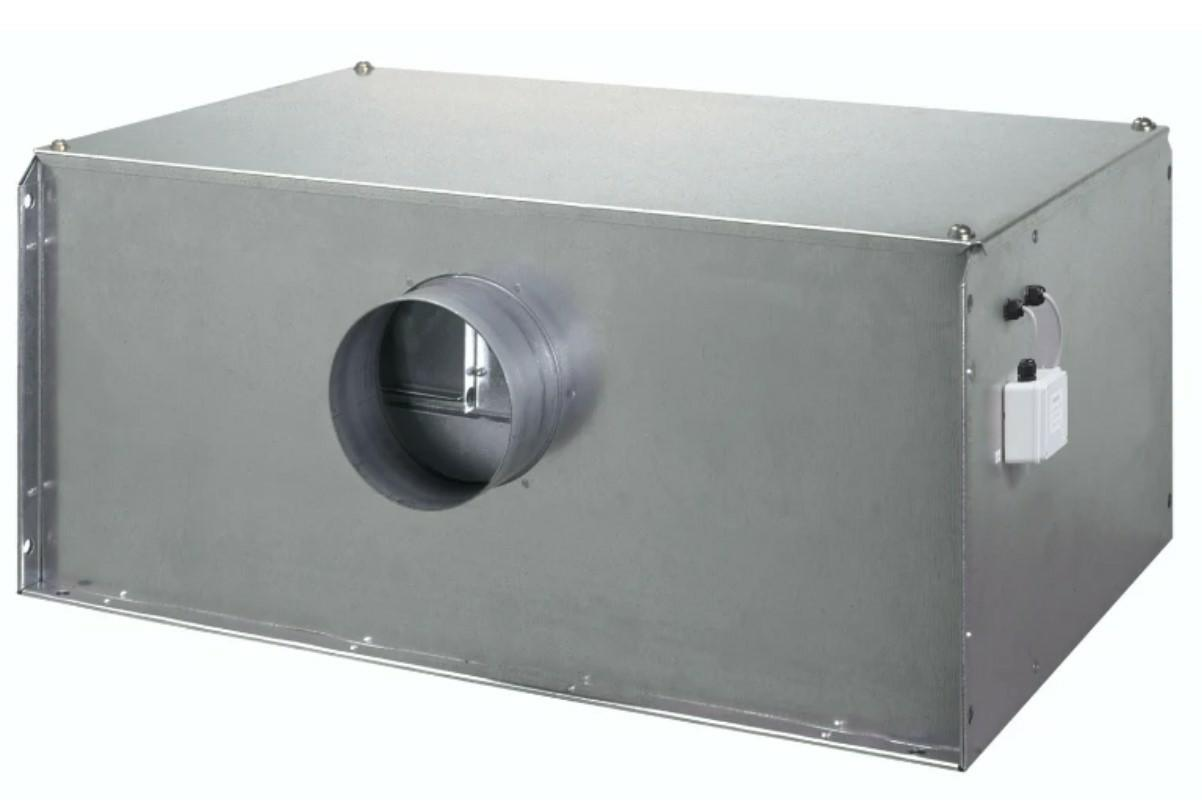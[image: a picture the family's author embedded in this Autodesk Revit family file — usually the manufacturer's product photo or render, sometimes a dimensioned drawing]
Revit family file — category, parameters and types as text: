
# Revit family: CADS_Vent-Axia_MechEquip_Fan_ATQ - EXTRACT
name_source: partatom
category: Mechanical Equipment
units: mm (PartAtom-declared; Revit-internal decimal feet)

## family parameters
Classification = None
Cut with Voids When Loaded = No
Host = Face
OmniClass Number = 23.75.35.17.11
OmniClass Title = Fans for Air Ductwork
Part Type = Normal
Room Calculation Point = No
Round Connector Dimension = Use Diameter
Shared = No

## types (9) — shared parameters
AirflowRateRange = 0.0 L/s
AssemblyPlace = UNKNOWN
AssetType = FIXED
Default Elevation = 1219 mm
DurationUnit = Year
ExteriorInsulation = No
Fitting Type = Ignore
GrossWeight = 0.00 kg
HasProtectiveEarth = No
IsExtendedWarranty = No
ManufacturerAddress = Fleming Way
Crawley 
RH10 9YX
Quantity = 1
RatedCurrent = 0 A
RatedVoltage = 0 V
Status = New
WorkingPressure = 0.0 Pa
zero-valued in all types: CADS_Index, CADS_Usage, ExpectedServiceLife, H, NumberOfPoles, OutOffset, W

## per-type parameters (varying)
| type | EBHoffset | EBVoffset | L | ModelNumber | ModelReference | NominalDiameter | NominalHeight | NominalLength | NominalWidth | Size | SpigotCLHeight | Type Image |
| ATQ10012D | 206 mm | 80 mm | 590 mm  [stored 1.9357 ft] | ATQ31512LD | TWIN ACOUSTIC BOX FAN, 315 DIA SPIGOTS | 100 mm  [stored 0.328084 ft] | 256 mm  [stored 0.839895 ft] | 610 mm  [stored 2.00131 ft] | 622 mm  [stored 2.04068 ft] | 935mm x892mm x426mm | 128 mm  [stored 0.419948 ft] | <None> |
| ATQ12512D | 206 mm | 80 mm | 590 mm  [stored 1.9357 ft] | ATQ12512D | TWIN ACOUSTIC BOX FAN, 125 DIA SPIGOTS | 125 mm  [stored 0.410105 ft] | 256 mm  [stored 0.839895 ft] | 610 mm  [stored 2.00131 ft] | 622 mm  [stored 2.04068 ft] | 610mm x622mm x256mm | 128 mm  [stored 0.419948 ft] | <None> |
| ATQ15012D | 206 mm | 80 mm | 590 mm  [stored 1.9357 ft] | ATQ15012D | TWIN ACOUSTIC BOX FAN, 150 DIA SPIGOTS | 150 mm | 256 mm  [stored 0.839895 ft] | 610 mm  [stored 2.00131 ft] | 622 mm  [stored 2.04068 ft] | 610mm x622mm x256mm | 128 mm  [stored 0.419948 ft] | <None> |
| ATQ16012D | 206 mm | 80 mm | 590 mm  [stored 1.9357 ft] | ATQ16012D | TWIN ACOUSTIC BOX FAN, 160 DIA SPIGOTS | 160 mm  [stored 0.524934 ft] | 256 mm  [stored 0.839895 ft] | 610 mm  [stored 2.00131 ft] | 622 mm  [stored 2.04068 ft] | 610mm x622mm x256mm | 128 mm  [stored 0.419948 ft] | <None> |
| ATQ20012D | 251 mm | 131 mm | 781 mm | ATQ20012D | TWIN ACOUSTIC BOX FAN, 200 DIA SPIGOTS | 200 mm  [stored 0.656168 ft] | 343 mm  [stored 1.12533 ft] | 801 mm  [stored 2.62795 ft] | 734 mm  [stored 2.40814 ft] | 801mm x734mm x343mm | 172 mm | <None> |
| ATQ25012D | 313 mm | 143 mm | 905 mm  [stored 2.96916 ft] | ATQ25012D | TWIN ACOUSTIC BOX FAN, 250 DIA SPIGOTS | 250 mm  [stored 0.82021 ft] | 354 mm  [stored 1.16142 ft] | 925 mm | 829 mm  [stored 2.71982 ft] | 925mm x829mm x354mm | 177 mm  [stored 0.580709 ft] | <None> |
| ATQ31512LD | 361 mm | 207 mm | 915 mm  [stored 3.00197 ft] | ATQ31512LD | TWIN ACOUSTIC BOX FAN, 315 DIA SPIGOTS | 315 mm  [stored 1.03346 ft] | 426 mm  [stored 1.39764 ft] | 935 mm | 892 mm  [stored 2.92651 ft] | 935mm x892mm x426mm | 213 mm  [stored 0.698819 ft] | <None> |
| ATQ31514HD | 375 mm | 285 mm | 1235 mm | ATQ31514HD | TWIN ACOUSTIC BOX FAN, 315 DIA SPIGOTS | 315 mm  [stored 1.03346 ft] | 536 mm | 1255 mm | 1176 mm | 1255mm x1176mm x536mm | 268 mm | <None> |
| ATQ40014D | 377 mm | 285 mm | 1235 mm | ATQ40014D | TWIN ACOUSTIC BOX FAN, 400 DIA SPIGOTS | 400 mm  [stored 1.31234 ft] | 536 mm | 1255 mm | 1176 mm | 1255mm x1176mm x536mm | 268 mm | CADS_Vent-Axia_MechEquip_Fan_ATQ.jpg |

note: [stored X ft] marks values corroborated as IEEE doubles in the binary element streams (Revit-internal decimal feet)

## geometry (parser evidence)
native form markers: Sweep x2
no freeform markers — native parametric forms only
